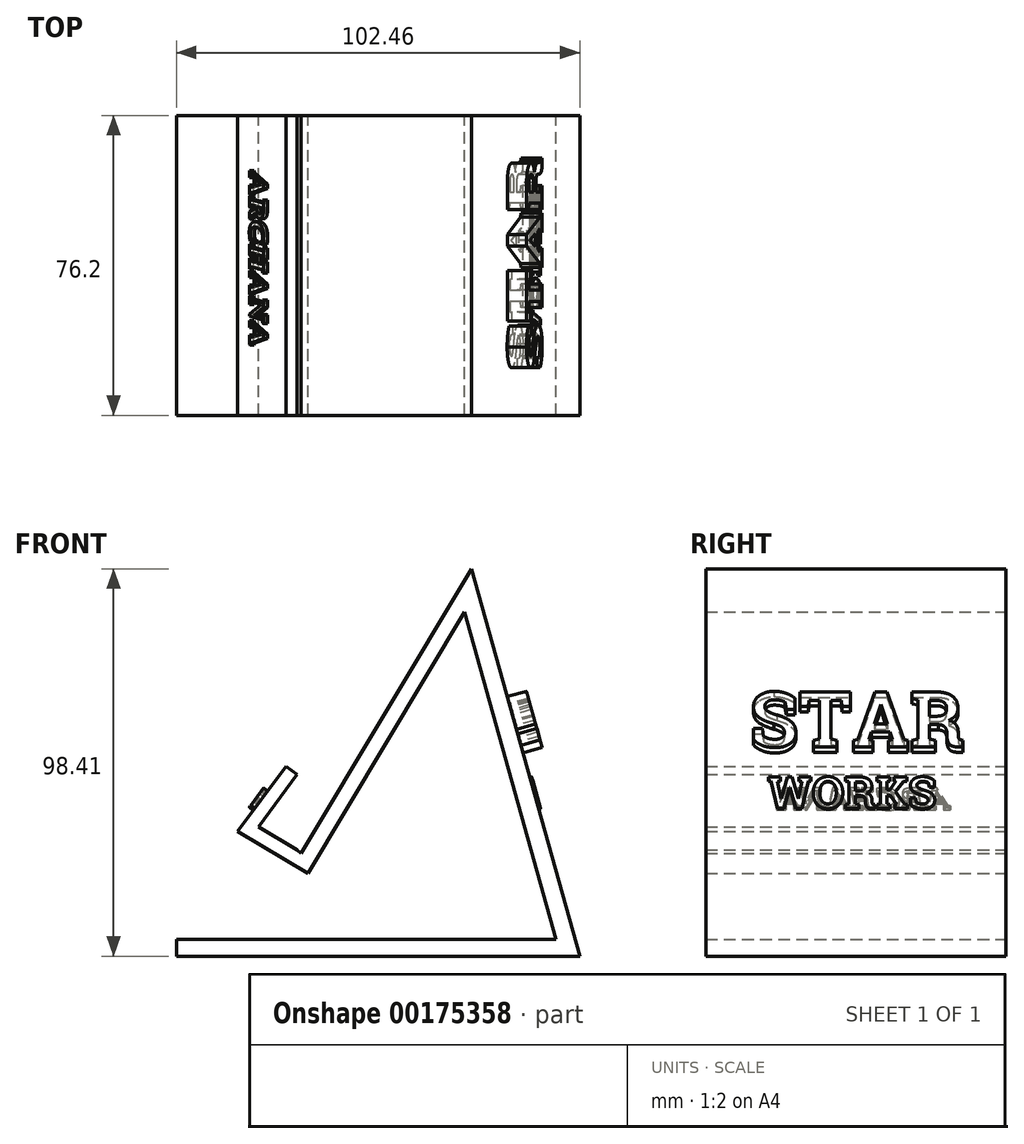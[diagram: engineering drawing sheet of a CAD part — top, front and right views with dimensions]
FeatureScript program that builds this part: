
annotation { "Feature Type Name" : "Feature", "Feature Type Description" : "" }
export const myFeature = defineFeature(function(context is Context, id is Id, definition is map)
    precondition{}
    {
        {
            var Q0;
            Q0=qCreatedBy(makeId("Front.planeOp"),FACE);
            var sketch = newSketch(context, id + "F0", { "sketchPlane" : qUnion([Q0])});
            skLineSegment(sketch, "E0", {"start": v(-46.91, -27.34) * mm, "end": v(49.5, -27.34) * mm});
            skLineSegment(sketch, "E1", {"start": v(-46.91, -27.34) * mm, "end": v(-46.91, -31.66) * mm});
            skLineSegment(sketch, "E2", {"start": v(-46.91, -31.66) * mm, "end": v(55.55, -31.66) * mm});
            skLineSegment(sketch, "E3", {"start": v(55.55, -31.66) * mm, "end": v(31.95, 52.67) * mm});
            skLineSegment(sketch, "E4", {"start": v(49.5, -27.34) * mm, "end": v(30.5, 40.58) * mm});
            skLineSegment(sketch, "E5", {"start": v(31.95, 52.67) * mm, "end": v(28, 66.75) * mm});
            skLineSegment(sketch, "E6", {"start": v(28, 66.75) * mm, "end": v(-13.53, -2.6) * mm});
            skLineSegment(sketch, "E7", {"start": v(30.5, 40.58) * mm, "end": v(27.11, 52.67) * mm});
            skLineSegment(sketch, "E8", {"start": v(27.11, 52.67) * mm, "end": v(26.26, 55.72) * mm});
            skLineSegment(sketch, "E9", {"start": v(26.26, 55.72) * mm, "end": v(-13.53, -10.7) * mm});
            skLineSegment(sketch, "E10", {"start": v(-13.53, -10.7) * mm, "end": v(-31.38, 0) * mm});
            skLineSegment(sketch, "E11", {"start": v(-31.38, 0) * mm, "end": v(-19.13, 16.6) * mm});
            skLineSegment(sketch, "E12", {"start": v(-19.13, 16.6) * mm, "end": v(-16.23, 14.45) * mm});
            skLineSegment(sketch, "E13", {"start": v(-16.23, 14.45) * mm, "end": v(-25.06, 2.47) * mm});
            skLineSegment(sketch, "E14", {"start": v(-25.06, 2.47) * mm, "end": v(-26.02, 1.18) * mm});
            skLineSegment(sketch, "E15", {"start": v(-26.02, 1.18) * mm, "end": v(-16.23, -4.68) * mm});
            skLineSegment(sketch, "E16", {"start": v(-13.53, -2.6) * mm, "end": v(-15.3, -5.55) * mm});
            skLineSegment(sketch, "E17", {"start": v(-16.23, -4.68) * mm, "end": v(-15.3, -5.55) * mm});
            skSolve(sketch);
        }
        {
            var Q0;
            Q0=makeQuery(id+"F0.imprint","IMPRINT",FACE,{"disambiguationData":[TD([[makeQuery(id+"F0.imprint","IMPRINT",EDGE,{"derivedFrom":sQuery(id+"F0.wireOp",EDGE,"E0")}),-1.0]])]});
            extrude(context, id + "F1", {"entities" : qUnion([Q0]), "depth" : 25.4 * mm});
        }
        {
            var Q0;
            Q0=makeQuery(id+"F1.opExtrude","CAP_FACE",FACE,{"disambiguationData":[OSD([sQuery(id+"F0.wireOp",EDGE,"E0"),sQuery(id+"F0.wireOp",EDGE,"E1"),sQuery(id+"F0.wireOp",EDGE,"E2"),sQuery(id+"F0.wireOp",EDGE,"E3"),sQuery(id+"F0.wireOp",EDGE,"E4"),sQuery(id+"F0.wireOp",EDGE,"E5"),sQuery(id+"F0.wireOp",EDGE,"E6"),sQuery(id+"F0.wireOp",EDGE,"E7"),sQuery(id+"F0.wireOp",EDGE,"E8"),sQuery(id+"F0.wireOp",EDGE,"E9"),sQuery(id+"F0.wireOp",EDGE,"E10"),sQuery(id+"F0.wireOp",EDGE,"E11"),sQuery(id+"F0.wireOp",EDGE,"E12"),sQuery(id+"F0.wireOp",EDGE,"E13"),sQuery(id+"F0.wireOp",EDGE,"E14"),sQuery(id+"F0.wireOp",EDGE,"E15"),sQuery(id+"F0.wireOp",EDGE,"E16"),sQuery(id+"F0.wireOp",EDGE,"E17")])],"isStart":false});
            extrude(context, id + "F2", {"entities" : qUnion([Q0]), "operationType" : NewBodyOperationType.ADD, "depth" : 50.8 * mm});
        }
        {
            var Q0;
            {var subQ0=sQuery(id+"F0.wireOp",EDGE,"E5");var subQ1=sQuery(id+"F0.wireOp",EDGE,"E3");Q0=makeQuery(id+"F2.boolean.opBoolean","MERGE",FACE,{"derivedFrom":[makeQuery(id+"F1.opExtrude","SWEPT_FACE",FACE,{"disambiguationData":[OSD([subQ1,subQ0])]}),makeQuery(id+"F2.opExtrude","SWEPT_FACE",FACE,{"disambiguationData":[OSD([subQ1,subQ0])]})]});}
            var sketch = newSketch(context, id + "F3", { "sketchPlane" : qUnion([Q0])});
            skText(sketch, "E18", { "text": "STAR", "fontName": "RobotoSlab-Bold.ttf"});
            const initialGuessF3  = {"E18": [-0.06504, 0.00834, 1, 0, 0.01464]};
            skSetInitialGuess(sketch, initialGuessF3);
            skSolve(sketch);
        }
        {
            var Q0;
            Q0 = qSketchRegion(id + "F3", true);
            extrude(context, id + "F4", {"entities" : qUnion([Q0]), "operationType" : NewBodyOperationType.ADD, "depth" : 5.08 * mm});
        }
        {
            var Q0;
            {var subQ12=sQuery(id+"F0.wireOp",EDGE,"E5");var subQ14=sQuery(id+"F0.wireOp",EDGE,"E3");var subQ15=sQuery(id+"F0.wireOp",EDGE,"E2");Q0=makeQuery(id+"F4.boolean.opBoolean","SPLIT",FACE,{"disambiguationData":[TD([makeQuery(id+"F1.opExtrude","SWEPT_FACE",FACE,{"disambiguationData":[OSD([subQ15])]})])],"derivedFrom":makeQuery(id+"F2.boolean.opBoolean","MERGE",FACE,{"derivedFrom":[makeQuery(id+"F1.opExtrude","SWEPT_FACE",FACE,{"disambiguationData":[OSD([subQ14,subQ12])]}),makeQuery(id+"F2.opExtrude","SWEPT_FACE",FACE,{"disambiguationData":[OSD([subQ14,subQ12])]})]})});}
            var sketch = newSketch(context, id + "F5", { "sketchPlane" : qUnion([Q0])});
            skText(sketch, "E19", { "text": "WORKS", "fontName": "RobotoSlab-Bold.ttf"});
            const initialGuessF5  = {"E19": [-0.06046, -0.0066, 1, 0, 0.00837]};
            skSetInitialGuess(sketch, initialGuessF5);
            skSolve(sketch);
        }
        {
            var Q0;
            Q0 = qSketchRegion(id + "F5", true);
            extrude(context, id + "F6", {"entities" : qUnion([Q0]), "operationType" : NewBodyOperationType.ADD, "depth" : 0.5 * mm});
        }
        {
            var Q0;
            {var subQ0=sQuery(id+"F0.wireOp",EDGE,"E11");Q0=makeQuery(id+"F2.boolean.opBoolean","MERGE",FACE,{"derivedFrom":[makeQuery(id+"F1.opExtrude","SWEPT_FACE",FACE,{"disambiguationData":[OSD([subQ0])]}),makeQuery(id+"F2.opExtrude","SWEPT_FACE",FACE,{"disambiguationData":[OSD([subQ0])]})]});}
            var sketch = newSketch(context, id + "F7", { "sketchPlane" : qUnion([Q0])});
            skText(sketch, "E20", { "text": "ARCHANA", "fontName": "Tinos-BoldItalic.ttf"});
            const initialGuessF7  = {"E20": [0.01448, -0.01186, 1, 0, 0.00658]};
            skSetInitialGuess(sketch, initialGuessF7);
            skSolve(sketch);
        }
        {
            var Q0;
            Q0 = qSketchRegion(id + "F7", true);
            extrude(context, id + "F8", {"entities" : qUnion([Q0]), "operationType" : NewBodyOperationType.ADD, "depth" : 1.27 * mm, "offsetDistance" : 25.4 * mm});
        }
    });
